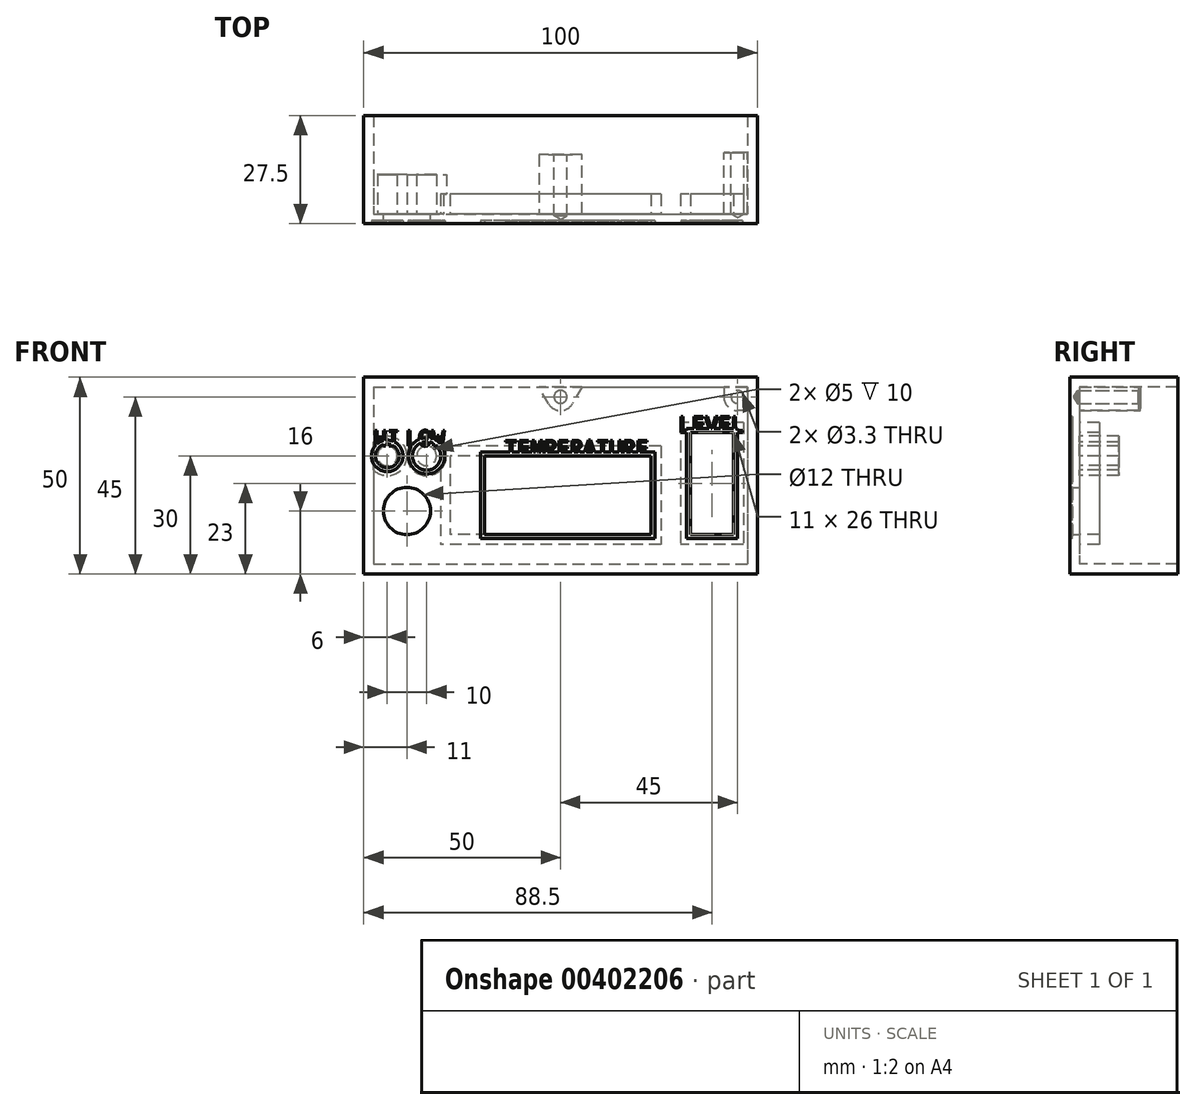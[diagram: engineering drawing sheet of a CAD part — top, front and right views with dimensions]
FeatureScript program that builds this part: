
annotation { "Feature Type Name" : "Feature", "Feature Type Description" : "" }
export const myFeature = defineFeature(function(context is Context, id is Id, definition is map)
    precondition{}
    {
        {
            assignVariable(context, id + "F0", {"name" : "FaceThickness", "anyValue" : 2.5});
        }
        {
            assignVariable(context, id + "F1", {"name" : "BoxDepth", "anyValue" : 25});
        }
        {
            var Q0;
            Q0=qCreatedBy(makeId("Front.planeOp"),FACE);
            var sketch = newSketch(context, id + "F2", { "sketchPlane" : qUnion([Q0])});
            skLineSegment(sketch, "E0.bottom", {"start": v(-50, 25) * mm, "end": v(50, 25) * mm});
            skLineSegment(sketch, "E0.top", {"start": v(-50, -25) * mm, "end": v(50, -25) * mm});
            skLineSegment(sketch, "E0.left", {"start": v(-50, 25) * mm, "end": v(-50, -25) * mm});
            skLineSegment(sketch, "E0.right", {"start": v(50, 25) * mm, "end": v(50, -25) * mm});
            skSolve(sketch);
        }
        {
            var Q0;
            Q0 = qSketchRegion(id + "F2", true);
            extrude(context, id + "F3", {"entities" : qUnion([Q0]), "oppositeDirection" : true, "depth" : (getVariable(context, 'FaceThickness')) * mm});
        }
        {
            var Q0;
            Q0=makeQuery(id+"F3.opExtrude","CAP_FACE",FACE,{"disambiguationData":[OSD([sQuery(id+"F2.wireOp",EDGE,"E0.bottom"),sQuery(id+"F2.wireOp",EDGE,"E0.top"),sQuery(id+"F2.wireOp",EDGE,"E0.left"),sQuery(id+"F2.wireOp",EDGE,"E0.right")])],"isStart":false});
            var sketch = newSketch(context, id + "F4", { "sketchPlane" : qUnion([Q0])});
            skLineSegment(sketch, "E1.bottom", {"start": v(-44, 11) * mm, "end": v(-33, 11) * mm});
            skLineSegment(sketch, "E1.top", {"start": v(-44, -15) * mm, "end": v(-33, -15) * mm});
            skLineSegment(sketch, "E1.left", {"start": v(-44, 11) * mm, "end": v(-44, -15) * mm});
            skLineSegment(sketch, "E1.right", {"start": v(-33, 11) * mm, "end": v(-33, -15) * mm});
            skLineSegment(sketch, "E2.0", {"start": v(-46.5, 13.5) * mm, "end": v(-30.5, 13.5) * mm});
            skLineSegment(sketch, "E2.1", {"start": v(-46.5, 13.5) * mm, "end": v(-46.5, -17.5) * mm});
            skLineSegment(sketch, "E2.2", {"start": v(-46.5, -17.5) * mm, "end": v(-30.5, -17.5) * mm});
            skLineSegment(sketch, "E2.3", {"start": v(-30.5, 13.5) * mm, "end": v(-30.5, -17.5) * mm});
            skSolve(sketch);
        }
        {
            var Q0;
            {var subQ0=sQuery(id+"F2.wireOp",EDGE,"E0.left");var subQ1=sQuery(id+"F2.wireOp",EDGE,"E0.top");var subQ2=sQuery(id+"F2.wireOp",EDGE,"E0.right");var subQ3=sQuery(id+"F2.wireOp",EDGE,"E0.bottom");Q0=makeQuery(id+"F6.boolean.opBoolean","SPLIT",FACE,{"disambiguationData":[TD([makeQuery(id+"F3.opExtrude","SWEPT_FACE",FACE,{"disambiguationData":[OSD([subQ3])]})])],"derivedFrom":makeQuery(id+"F3.opExtrude","CAP_FACE",FACE,{"disambiguationData":[OSD([subQ3,subQ1,subQ0,subQ2])],"isStart":false})});}
            var sketch = newSketch(context, id + "F5", { "sketchPlane" : qUnion([Q0])});
            skLineSegment(sketch, "E3.bottom", {"start": v(-23, 5) * mm, "end": v(28, 5) * mm});
            skLineSegment(sketch, "E3.top", {"start": v(-23, -15) * mm, "end": v(28, -15) * mm});
            skLineSegment(sketch, "E3.left", {"start": v(-23, 5) * mm, "end": v(-23, -15) * mm});
            skLineSegment(sketch, "E3.right", {"start": v(28, 5) * mm, "end": v(28, -15) * mm});
            skLineSegment(sketch, "E4.0", {"start": v(-25.5, 7.5) * mm, "end": v(30.5, 7.5) * mm});
            skLineSegment(sketch, "E4.1", {"start": v(-25.5, 7.5) * mm, "end": v(-25.5, -17.5) * mm});
            skLineSegment(sketch, "E4.2", {"start": v(-25.5, -17.5) * mm, "end": v(30.5, -17.5) * mm});
            skLineSegment(sketch, "E4.3", {"start": v(30.5, 7.5) * mm, "end": v(30.5, -17.5) * mm});
            skSolve(sketch);
        }
        {
            var Q0;
            Q0 = qSketchRegion(id + "F4", true);
            var Q1;
            Q1 = qSketchRegion(id + "F5", true);
            extrude(context, id + "F6", {"entities" : qUnion([Q0, Q1]), "operationType" : NewBodyOperationType.ADD, "depth" : 5 * mm});
        }
        {
            var Q0;
            Q0=makeQuery(id+"F6.opExtrude","SWEPT_FACE",FACE,{"disambiguationData":[OSD([sQuery(id+"F5.wireOp",EDGE,"E4.3")])]});
            cPlane(context, id + "F7", {"entities" : qUnion([Q0]), "cplaneType" : CPlaneType.OFFSET, "offset" : (17 / 2) * mm, "width" : 150 * mm, "height" : 150 * mm});
        }
        {
            var Q0;
            {var subQ0=sQuery(id+"F2.wireOp",EDGE,"E0.bottom");var subQ1=sQuery(id+"F2.wireOp",EDGE,"E0.right");var subQ2=sQuery(id+"F2.wireOp",EDGE,"E0.top");var subQ3=sQuery(id+"F2.wireOp",EDGE,"E0.left");Q0=makeQuery(id+"F6.boolean.opBoolean","SPLIT",FACE,{"disambiguationData":[TD([makeQuery(id+"F3.opExtrude","SWEPT_FACE",FACE,{"disambiguationData":[OSD([subQ0])]})])],"derivedFrom":makeQuery(id+"F3.opExtrude","CAP_FACE",FACE,{"disambiguationData":[OSD([subQ0,subQ2,subQ3,subQ1])],"isStart":false})});}
            var sketch = newSketch(context, id + "F8", { "sketchPlane" : qUnion([Q0])});
            skPoint(sketch, "E5", {"position": v(39, -9) * mm});
            skSolve(sketch);
        }
        {
            var Q0;
            Q0=sQuery(id+"F8.wireOp",VERTEX,"E5");
            var Q1;
            Q1=makeQuery(id+"F3.opExtrude","SWEPT_BODY",BODY,{"disambiguationData":[OSD([sQuery(id+"F2.wireOp",EDGE,"E0.bottom"),sQuery(id+"F2.wireOp",EDGE,"E0.top"),sQuery(id+"F2.wireOp",EDGE,"E0.left"),sQuery(id+"F2.wireOp",EDGE,"E0.right")])]});
            hole(context, id + "F9", {"style" : HoleStyle.SIMPLE, "endStyle" : HoleEndStyle.THROUGH, "holeDiameter" : 12 * mm, "isTappedThrough" : true, "tappedDepth" : 12 * mm, "tapClearance" : 3, "locations" : qUnion([Q0]), "scope" : qUnion([Q1])});
        }
        {
            var Q0;
            {var subQ0=sQuery(id+"F2.wireOp",EDGE,"E0.bottom");var subQ1=sQuery(id+"F2.wireOp",EDGE,"E0.right");var subQ2=sQuery(id+"F2.wireOp",EDGE,"E0.top");var subQ3=sQuery(id+"F2.wireOp",EDGE,"E0.left");Q0=makeQuery(id+"F6.boolean.opBoolean","SPLIT",FACE,{"disambiguationData":[TD([makeQuery(id+"F3.opExtrude","SWEPT_FACE",FACE,{"disambiguationData":[OSD([subQ0])]})])],"derivedFrom":makeQuery(id+"F3.opExtrude","CAP_FACE",FACE,{"disambiguationData":[OSD([subQ0,subQ2,subQ3,subQ1])],"isStart":false})});}
            var sketch = newSketch(context, id + "F10", { "sketchPlane" : qUnion([Q0])});
            skCircle(sketch, "E6", {"center": v(34, 5) * mm, "radius": 2.5 * mm});
            skCircle(sketch, "E7", {"center": v(34, 5) * mm, "radius": 5 * mm});
            skSolve(sketch);
        }
        {
            var Q0;
            Q0=makeQuery(id+"F8.imprint","IMPRINT",FACE,{"disambiguationData":[TD([[makeQuery(id+"F8.imprint","IMPRINT",EDGE,{"derivedFrom":makeQuery(id+"F3.opExtrude","CAP_EDGE",EDGE,{"disambiguationData":[OSD([sQuery(id+"F2.wireOp",EDGE,"E0.bottom")])],"isStart":false})}),1.0]])]});
            var sketch = newSketch(context, id + "F11", { "sketchPlane" : qUnion([Q0])});
            skCircle(sketch, "E8", {"center": v(44, 5) * mm, "radius": 2.5 * mm});
            skCircle(sketch, "E9", {"center": v(44, 5) * mm, "radius": 5 * mm});
            skSolve(sketch);
        }
        {
            var Q0;
            Q0 = qSketchRegion(id + "F10", true);
            var Q1;
            Q1 = qSketchRegion(id + "F11", true);
            extrude(context, id + "F12", {"entities" : qUnion([Q0, Q1]), "operationType" : NewBodyOperationType.ADD, "depth" : 10 * mm});
        }
        {
            var Q0;
            {var subQ2=sQuery(id+"F2.wireOp",EDGE,"E0.bottom");var subQ3=makeQuery(id+"F3.opExtrude","SWEPT_FACE",FACE,{"disambiguationData":[OSD([subQ2])]});var subQ5=sQuery(id+"F2.wireOp",EDGE,"E0.right");var subQ9=sQuery(id+"F2.wireOp",EDGE,"E0.top");var subQ12=sQuery(id+"F2.wireOp",EDGE,"E0.left");Q0=makeQuery(id+"F12.boolean.opBoolean","SPLIT",FACE,{"disambiguationData":[TD([subQ3])],"derivedFrom":makeQuery(id+"F6.boolean.opBoolean","SPLIT",FACE,{"disambiguationData":[TD([subQ3])],"derivedFrom":makeQuery(id+"F3.opExtrude","CAP_FACE",FACE,{"disambiguationData":[OSD([subQ2,subQ9,subQ12,subQ5])],"isStart":false})})});}
            var sketch = newSketch(context, id + "F13", { "sketchPlane" : qUnion([Q0])});
            skLineSegment(sketch, "E10.0", {"start": v(-50, 25) * mm, "end": v(-50, -25) * mm});
            skLineSegment(sketch, "E11.0", {"start": v(50, 25) * mm, "end": v(-50, 25) * mm});
            skLineSegment(sketch, "E12.0", {"start": v(50, 25) * mm, "end": v(50, -25) * mm});
            skLineSegment(sketch, "E13.0", {"start": v(50, -25) * mm, "end": v(-50, -25) * mm});
            skLineSegment(sketch, "E14.0", {"start": v(-47.5, 22.5) * mm, "end": v(-47.5, -22.5) * mm});
            skLineSegment(sketch, "E14.1", {"start": v(47.5, 22.5) * mm, "end": v(-47.5, 22.5) * mm});
            skLineSegment(sketch, "E14.2", {"start": v(47.5, 22.5) * mm, "end": v(47.5, -22.5) * mm});
            skLineSegment(sketch, "E14.3", {"start": v(47.5, -22.5) * mm, "end": v(-47.5, -22.5) * mm});
            skSolve(sketch);
        }
        {
            var Q0;
            Q0 = qSketchRegion(id + "F13", true);
            extrude(context, id + "F14", {"entities" : qUnion([Q0]), "operationType" : NewBodyOperationType.ADD, "depth" : (getVariable(context, 'BoxDepth')) * mm});
        }
        {
            var Q0;
            Q0=makeQuery(id+"F3.opExtrude","CAP_FACE",FACE,{"disambiguationData":[OSD([sQuery(id+"F2.wireOp",EDGE,"E0.bottom"),sQuery(id+"F2.wireOp",EDGE,"E0.top"),sQuery(id+"F2.wireOp",EDGE,"E0.left"),sQuery(id+"F2.wireOp",EDGE,"E0.right")])],"isStart":true});
            var sketch = newSketch(context, id + "F15", { "sketchPlane" : qUnion([Q0])});
            skArc(sketch, "E15", {"start": v(41.5, 20) * mm, "mid": v(42.53, 17.53) * mm, "end": v(45, 16.5) * mm});
            skLineSegment(sketch, "E16", {"start": v(50, 16.5) * mm, "end": v(45, 16.5) * mm});
            skLineSegment(sketch, "E17", {"start": v(41.5, 25) * mm, "end": v(41.5, 20) * mm});
            skLineSegment(sketch, "E18", {"start": v(50, 16.5) * mm, "end": v(50, 25) * mm});
            skLineSegment(sketch, "E19", {"start": v(50, 25) * mm, "end": v(41.5, 25) * mm});
            skSolve(sketch);
        }
        {
            var Q0;
            Q0 = qSketchRegion(id + "F15", true);
            extrude(context, id + "F16", {"entities" : qUnion([Q0]), "operationType" : NewBodyOperationType.ADD, "oppositeDirection" : true, "depth" : (getVariable(context, 'BoxDepth') - 7) * mm});
        }
        {
            var Q0;
            Q0=qCreatedBy(makeId("Top.planeOp"),FACE);
            var Q1;
            Q1=sQuery(id+"F15.wireOp",VERTEX,"E15.center");
            cPlane(context, id + "F17", {"entities" : qUnion([Q0, Q1]), "cplaneType" : CPlaneType.PLANE_POINT, "offset" : 25 * mm, "width" : 150 * mm, "height" : 150 * mm});
        }
        {
            var Q0;
            Q0=makeQuery(id+"F3.opExtrude","CAP_FACE",FACE,{"disambiguationData":[OSD([sQuery(id+"F2.wireOp",EDGE,"E0.bottom"),sQuery(id+"F2.wireOp",EDGE,"E0.top"),sQuery(id+"F2.wireOp",EDGE,"E0.left"),sQuery(id+"F2.wireOp",EDGE,"E0.right")])],"isStart":true});
            var sketch = newSketch(context, id + "F18", { "sketchPlane" : qUnion([Q0])});
            skArc(sketch, "E20", {"start": v(-3.03, 18.25) * mm, "mid": v(0, 16.5) * mm, "end": v(3.03, 18.25) * mm});
            skLineSegment(sketch, "E21", {"start": v(6.93, 25) * mm, "end": v(3.03, 18.25) * mm});
            skLineSegment(sketch, "E22", {"start": v(-3.03, 18.25) * mm, "end": v(-6.93, 25) * mm});
            skLineSegment(sketch, "E23", {"start": v(6.93, 25) * mm, "end": v(-6.93, 25) * mm});
            skSolve(sketch);
        }
        {
            var Q0;
            Q0=makeQuery(id+"F16.opExtrude","CAP_FACE",FACE,{"disambiguationData":[OSD([sQuery(id+"F15.wireOp",EDGE,"E15"),sQuery(id+"F15.wireOp",EDGE,"E16"),sQuery(id+"F15.wireOp",EDGE,"E17"),sQuery(id+"F15.wireOp",EDGE,"E18"),sQuery(id+"F15.wireOp",EDGE,"E19")])],"isStart":false});
            var sketch = newSketch(context, id + "F19", { "sketchPlane" : qUnion([Q0])});
            skPoint(sketch, "E24.0", {"position": v(-45, 20) * mm});
            skPoint(sketch, "E25.0", {"position": v(0, 20) * mm});
            skSolve(sketch);
        }
        {
            var Q0;
            Q0 = qSketchRegion(id + "F18", true);
            var Q1;
            Q1 = qConstructionFilter(qBodyType(qCreatedBy(id + "F18" ,EDGE), BodyType.WIRE), ConstructionObject.NO);
            extrude(context, id + "F20", {"entities" : qUnion([Q0]), "operationType" : NewBodyOperationType.ADD, "surfaceEntities" : qUnion([Q1]), "oppositeDirection" : true, "depth" : (getVariable(context, 'BoxDepth') - 5 - getVariable(context, 'FaceThickness')) * mm});
        }
        {
            var Q0;
            Q0=sQuery(id+"F19.wireOp",VERTEX,"E24.0");
            var Q1;
            Q1=sQuery(id+"F19.wireOp",VERTEX,"E25.0");
            var Q2;
            Q2=makeQuery(id+"F3.opExtrude","SWEPT_BODY",BODY,{"disambiguationData":[OSD([sQuery(id+"F2.wireOp",EDGE,"E0.bottom"),sQuery(id+"F2.wireOp",EDGE,"E0.top"),sQuery(id+"F2.wireOp",EDGE,"E0.left"),sQuery(id+"F2.wireOp",EDGE,"E0.right")])]});
            hole(context, id + "F21", {"style" : HoleStyle.SIMPLE, "endStyle" : HoleEndStyle.BLIND, "standardTappedOrClearance" : lookupTablePath({ "standard" : "ISO", "engagement" : "75%", "pitch" : "0.7 mm", "size" : "M4", "type" : "Tapped" }), "standardBlindInLast" : lookupTablePath({ "standard" : "ISO", "engagement" : "75%", "pitch" : "0.7 mm", "size" : "M4", "type" : "Tapped" }), "holeDiameter" : 3.3 * mm, "showTappedDepth" : true, "holeDepth" : (getVariable(context, 'BoxDepth') - 7 - getVariable(context, 'FaceThickness')) * mm, "isTappedThrough" : true, "tappedDepth" : 38.4 * mm, "tapClearance" : 3, "locations" : qUnion([Q0, Q1]), "scope" : qUnion([Q2]), "majorDiameter" : 4 * mm});
        }
        {
            var Q0;
            Q0=makeQuery(id+"F3.opExtrude","CAP_FACE",FACE,{"disambiguationData":[OSD([sQuery(id+"F2.wireOp",EDGE,"E0.bottom"),sQuery(id+"F2.wireOp",EDGE,"E0.top"),sQuery(id+"F2.wireOp",EDGE,"E0.left"),sQuery(id+"F2.wireOp",EDGE,"E0.right")])],"isStart":true});
            var sketch = newSketch(context, id + "F22", { "sketchPlane" : qUnion([Q0])});
            skPoint(sketch, "E26.0", {"position": v(-44, 5) * mm});
            skPoint(sketch, "E27.0", {"position": v(-34, 5) * mm});
            skSolve(sketch);
        }
        {
            var Q0;
            Q0=sQuery(id+"F11.wireOp",VERTEX,"E8.center");
            var Q1;
            Q1=sQuery(id+"F22.wireOp",VERTEX,"E26.0");
            var Q2;
            Q2=sQuery(id+"F10.wireOp",VERTEX,"E6.center");
            cPlane(context, id + "F23", {"entities" : qUnion([Q0, Q1, Q2]), "cplaneType" : CPlaneType.THREE_POINT, "offset" : 25 * mm, "width" : 150 * mm, "height" : 150 * mm});
        }
        {
            var Q0;
            Q0=qCreatedBy(id+"F23.planeOp",FACE);
            cPlane(context, id + "F24", {"entities" : qUnion([Q0]), "cplaneType" : CPlaneType.OFFSET, "offset" : (2.5 + 4) * mm, "oppositeDirection" : true, "width" : 150 * mm, "height" : 150 * mm});
        }
        {
            var Q0;
            Q0=makeQuery(id+"F6.opExtrude","SWEPT_FACE",FACE,{"disambiguationData":[OSD([sQuery(id+"F5.wireOp",EDGE,"E3.bottom")])]});
            cPlane(context, id + "F25", {"entities" : qUnion([Q0]), "cplaneType" : CPlaneType.OFFSET, "offset" : 4 * mm, "oppositeDirection" : true, "width" : 150 * mm, "height" : 150 * mm});
        }
        {
            var Q0;
            Q0=makeQuery(id+"F6.opExtrude","SWEPT_FACE",FACE,{"disambiguationData":[OSD([sQuery(id+"F4.wireOp",EDGE,"E1.bottom")])]});
            cPlane(context, id + "F26", {"entities" : qUnion([Q0]), "cplaneType" : CPlaneType.OFFSET, "offset" : 4 * mm, "oppositeDirection" : true, "width" : 150 * mm, "height" : 150 * mm});
        }
        {
            var Q0;
            Q0=makeQuery(id+"F6.opExtrude","SWEPT_FACE",FACE,{"disambiguationData":[OSD([sQuery(id+"F5.wireOp",EDGE,"E3.left")])]});
            cPlane(context, id + "F27", {"entities" : qUnion([Q0]), "cplaneType" : CPlaneType.OFFSET, "offset" : (50 / 4 * 3 / 2) * mm, "width" : 150 * mm, "height" : 150 * mm});
        }
        {
            var Q0;
            Q0=qCreatedBy(makeId("Front.planeOp"),FACE);
            var sketch = newSketch(context, id + "F28", { "sketchPlane" : qUnion([Q0])});
            skText(sketch, "E28", { "text": "HI", "fontName": "DroidSansMono.ttf"});
            skText(sketch, "E29", { "text": "LOW", "fontName": "DroidSansMono.ttf"});
            skText(sketch, "E30", { "text": "TEMPERATURE", "fontName": "DroidSansMono.ttf"});
            skText(sketch, "E31", { "text": "LEVEL", "fontName": "DroidSansMono.ttf"});
            const initialGuessF28  = {"E28": [-0.04744, 0.0075, 1, 0, 0.004], "E29": [-0.03941, 0.0075, 1, 0, 0.004], "E30": [-0.01427, 0.005, 1, 0, 0.004], "E31": [0.03004, 0.011, 1, 0, 0.004]};
            skSetInitialGuess(sketch, initialGuessF28);
            skSolve(sketch);
        }
        {
            var Q0;
            {var subQ0=sQuery(id+"F2.wireOp",EDGE,"E0.left");var subQ1=sQuery(id+"F2.wireOp",EDGE,"E0.top");var subQ2=sQuery(id+"F2.wireOp",EDGE,"E0.right");var subQ3=sQuery(id+"F2.wireOp",EDGE,"E0.bottom");Q0=makeQuery(id+"F30.boolean.opBoolean","SPLIT",FACE,{"disambiguationData":[TD([makeQuery(id+"F3.opExtrude","SWEPT_FACE",FACE,{"disambiguationData":[OSD([subQ3])]})])],"derivedFrom":makeQuery(id+"F3.opExtrude","CAP_FACE",FACE,{"disambiguationData":[OSD([subQ3,subQ1,subQ0,subQ2])],"isStart":true})});}
            var sketch = newSketch(context, id + "F29", { "sketchPlane" : qUnion([Q0])});
            skLineSegment(sketch, "E32.0.0", {"start": v(-19.25, 5) * mm, "end": v(-28, 5) * mm, "construction": true});
            skLineSegment(sketch, "E33.0.0", {"start": v(-28, -15) * mm, "end": v(-19.25, -15) * mm, "construction": true});
            skLineSegment(sketch, "E34.0.0", {"start": v(44, -15) * mm, "end": v(44, 11) * mm});
            skLineSegment(sketch, "E34.0.2", {"start": v(44, 11) * mm, "end": v(44, -15) * mm});
            skLineSegment(sketch, "E35.0.0", {"start": v(33, -15) * mm, "end": v(44, -15) * mm});
            skLineSegment(sketch, "E35.0.2", {"start": v(44, -15) * mm, "end": v(33, -15) * mm});
            skLineSegment(sketch, "E36.0.0", {"start": v(33, 11) * mm, "end": v(33, -15) * mm});
            skLineSegment(sketch, "E36.0.2", {"start": v(33, -15) * mm, "end": v(33, 11) * mm});
            skLineSegment(sketch, "E37.0.0", {"start": v(44, 11) * mm, "end": v(33, 11) * mm});
            skLineSegment(sketch, "E37.0.2", {"start": v(33, 11) * mm, "end": v(44, 11) * mm});
            skLineSegment(sketch, "E38", {"start": v(23, -15) * mm, "end": v(23, 5) * mm});
            skPoint(sketch, "E39.orphan", {"position": v(-28, 5) * mm});
            skPoint(sketch, "E40.orphan", {"position": v(-28, -15) * mm});
            skPoint(sketch, "E33.0.2.start.orphan", {"position": v(23, -15) * mm});
            skLineSegment(sketch, "E41", {"start": v(-19.25, 5) * mm, "end": v(-19.25, -15) * mm});
            skPoint(sketch, "E32.0.2.end.orphan", {"position": v(23, 5) * mm});
            skLineSegment(sketch, "E42", {"start": v(23, 5) * mm, "end": v(-19.25, 5) * mm});
            skLineSegment(sketch, "E43", {"start": v(23, -15) * mm, "end": v(-19.25, -15) * mm});
            skPoint(sketch, "E44.0", {"position": v(-44, 5) * mm});
            skPoint(sketch, "E45.0", {"position": v(-34, 5) * mm});
            skCircle(sketch, "E46", {"center": v(-44, 5) * mm, "radius": 3 * mm});
            skCircle(sketch, "E47", {"center": v(-34, 5) * mm, "radius": 3.6 * mm});
            skCircle(sketch, "E48.0", {"center": v(-44, 5) * mm, "radius": 4 * mm});
            skCircle(sketch, "E49.0", {"center": v(-34, 5) * mm, "radius": 4.6 * mm});
            skLineSegment(sketch, "E50.0", {"start": v(32, -16) * mm, "end": v(32, 12) * mm});
            skLineSegment(sketch, "E50.1", {"start": v(45, -16) * mm, "end": v(32, -16) * mm});
            skLineSegment(sketch, "E50.2", {"start": v(45, 12) * mm, "end": v(45, -16) * mm});
            skLineSegment(sketch, "E50.3", {"start": v(32, 12) * mm, "end": v(45, 12) * mm});
            skLineSegment(sketch, "E51.0", {"start": v(24, 6) * mm, "end": v(-20.25, 6) * mm});
            skLineSegment(sketch, "E51.1", {"start": v(24, -16) * mm, "end": v(24, 6) * mm});
            skLineSegment(sketch, "E51.2", {"start": v(24, -16) * mm, "end": v(-20.25, -16) * mm});
            skLineSegment(sketch, "E51.3", {"start": v(-20.25, 6) * mm, "end": v(-20.25, -16) * mm});
            skSolve(sketch);
        }
        {
            var Q0;
            Q0 = qSketchRegion(id + "F28", true);
            var Q1;
            Q1 = qSketchRegion(id + "F29", true);
            extrude(context, id + "F30", {"entities" : qUnion([Q0, Q1]), "operationType" : NewBodyOperationType.REMOVE, "oppositeDirection" : true, "depth" : .75 * mm});
        }
    });
